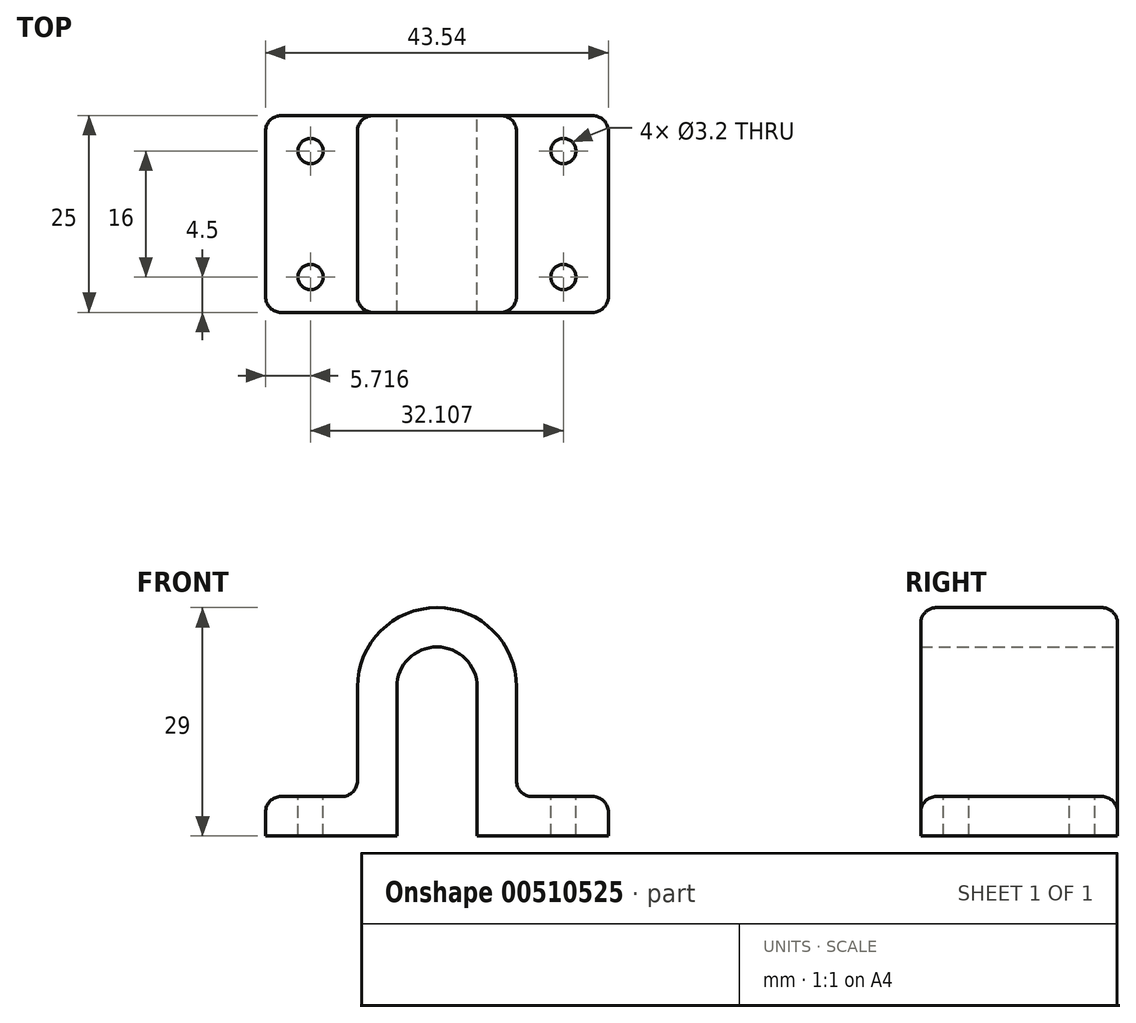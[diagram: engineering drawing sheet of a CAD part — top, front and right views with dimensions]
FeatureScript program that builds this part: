
annotation { "Feature Type Name" : "Feature", "Feature Type Description" : "" }
export const myFeature = defineFeature(function(context is Context, id is Id, definition is map)
    precondition{}
    {
        {
            var Q0;
            Q0=qCreatedBy(makeId("Front.planeOp"),FACE);
            var sketch = newSketch(context, id + "F0", { "sketchPlane" : qUnion([Q0])});
            skArc(sketch, "E0", {"start": v(5.1, 0) * mm, "mid": v(0, 5.1) * mm, "end": v(-5.1, 0) * mm});
            skLineSegment(sketch, "E1", {"start": v(-5.1, 0) * mm, "end": v(-5.1, -13.9) * mm});
            skLineSegment(sketch, "E2", {"start": v(5.1, 0) * mm, "end": v(5.1, -13.9) * mm});
            skLineSegment(sketch, "E3", {"start": v(12.1, -13.9) * mm, "end": v(19.77, -13.9) * mm});
            skLineSegment(sketch, "E4", {"start": v(21.77, -15.9) * mm, "end": v(21.77, -18.9) * mm});
            skLineSegment(sketch, "E5", {"start": v(21.77, -18.9) * mm, "end": v(5.1, -18.9) * mm});
            skLineSegment(sketch, "E6", {"start": v(-21.77, -18.9) * mm, "end": v(-21.77, -15.9) * mm});
            skLineSegment(sketch, "E7", {"start": v(-19.77, -13.9) * mm, "end": v(-12.1, -13.9) * mm});
            skLineSegment(sketch, "E8.0", {"start": v(-10.1, 0) * mm, "end": v(-10.1, -11.9) * mm});
            skArc(sketch, "E8.1", {"start": v(10.1, 0) * mm, "mid": v(0, 10.1) * mm, "end": v(-10.1, 0) * mm});
            skLineSegment(sketch, "E8.2", {"start": v(10.1, 0) * mm, "end": v(10.1, -11.9) * mm});
            skLineSegment(sketch, "E9", {"start": v(-5.1, -13.9) * mm, "end": v(-5.1, -18.9) * mm});
            skPoint(sketch, "E10.endSnap0", {"position": v(0, -18.9) * mm});
            skLineSegment(sketch, "E11", {"start": v(5.1, -18.9) * mm, "end": v(5.1, -13.9) * mm});
            skLineSegment(sketch, "E12.trimOffspring", {"start": v(-5.1, -18.9) * mm, "end": v(-21.77, -18.9) * mm});
            skPoint(sketch, "E13.visualSharp", {"position": v(-21.77, -13.9) * mm});
            skArc(sketch, "E13.filletArc", {"start": v(-19.77, -13.9) * mm, "mid": v(-21.18, -14.49) * mm, "end": v(-21.77, -15.9) * mm});
            skPoint(sketch, "E14.visualSharp", {"position": v(21.77, -13.9) * mm});
            skArc(sketch, "E14.filletArc", {"start": v(21.77, -15.9) * mm, "mid": v(21.18, -14.49) * mm, "end": v(19.77, -13.9) * mm});
            skPoint(sketch, "E15.visualSharp", {"position": v(-10.1, -13.9) * mm});
            skArc(sketch, "E15.filletArc", {"start": v(-12.1, -13.9) * mm, "mid": v(-10.69, -13.31) * mm, "end": v(-10.1, -11.9) * mm});
            skPoint(sketch, "E16.visualSharp", {"position": v(10.1, -13.9) * mm});
            skArc(sketch, "E16.filletArc", {"start": v(10.1, -11.9) * mm, "mid": v(10.69, -13.31) * mm, "end": v(12.1, -13.9) * mm});
            skSolve(sketch);
        }
        {
            var Q0;
            Q0 = qSketchRegion(id + "F0", true);
            extrude(context, id + "F1", {"entities" : qUnion([Q0]), "depth" : 25 * mm});
        }
        {
            var Q0;
            Q0=makeQuery(id+"F1.opExtrude","SWEPT_FACE",FACE,{"disambiguationData":[OSD([sQuery(id+"F0.wireOp",EDGE,"E3")])]});
            var sketch = newSketch(context, id + "F2", { "sketchPlane" : qUnion([Q0])});
            skCircle(sketch, "E17", {"center": v(16.05, -20.5) * mm, "radius": 1.6 * mm});
            skCircle(sketch, "E18", {"center": v(16.05, -4.5) * mm, "radius": 1.6 * mm});
            skCircle(sketch, "E19.MirrorC", {"center": v(-16.05, -4.5) * mm, "radius": 1.6 * mm});
            skCircle(sketch, "E20.MirrorC", {"center": v(-16.05, -20.5) * mm, "radius": 1.6 * mm});
            skLineSegment(sketch, "E21", {"start": v(27.8, -12.5) * mm, "end": v(-28.62, -12.5) * mm, "construction": true});
            skPoint(sketch, "E21.startSnap0", {"position": v(19.77, -12.5) * mm});
            skPoint(sketch, "E21.endSnap0", {"position": v(19.77, -12.5) * mm});
            skSolve(sketch);
        }
        {
            var Q0;
            Q0 = qSketchRegion(id + "F2", true);
            extrude(context, id + "F3", {"entities" : qUnion([Q0]), "operationType" : NewBodyOperationType.REMOVE, "oppositeDirection" : true, "depth" : 25 * mm});
        }
        {
            var Q0;
            Q0=makeQuery(id+"F1.opExtrude","CAP_EDGE",EDGE,{"disambiguationData":[OSD([sQuery(id+"F0.wireOp",EDGE,"E8.0")])],"isStart":false});
            var Q1;
            Q1=makeQuery(id+"F1.opExtrude","CAP_EDGE",EDGE,{"disambiguationData":[OSD([sQuery(id+"F0.wireOp",EDGE,"E8.0")])],"isStart":true});
            fillet(context, id + "F4", {"entities" : qUnion([Q0, Q1]), "radius" : 2 * mm, "tangentPropagation" : true, "allowEdgeOverflow" : false});
        }
    });
